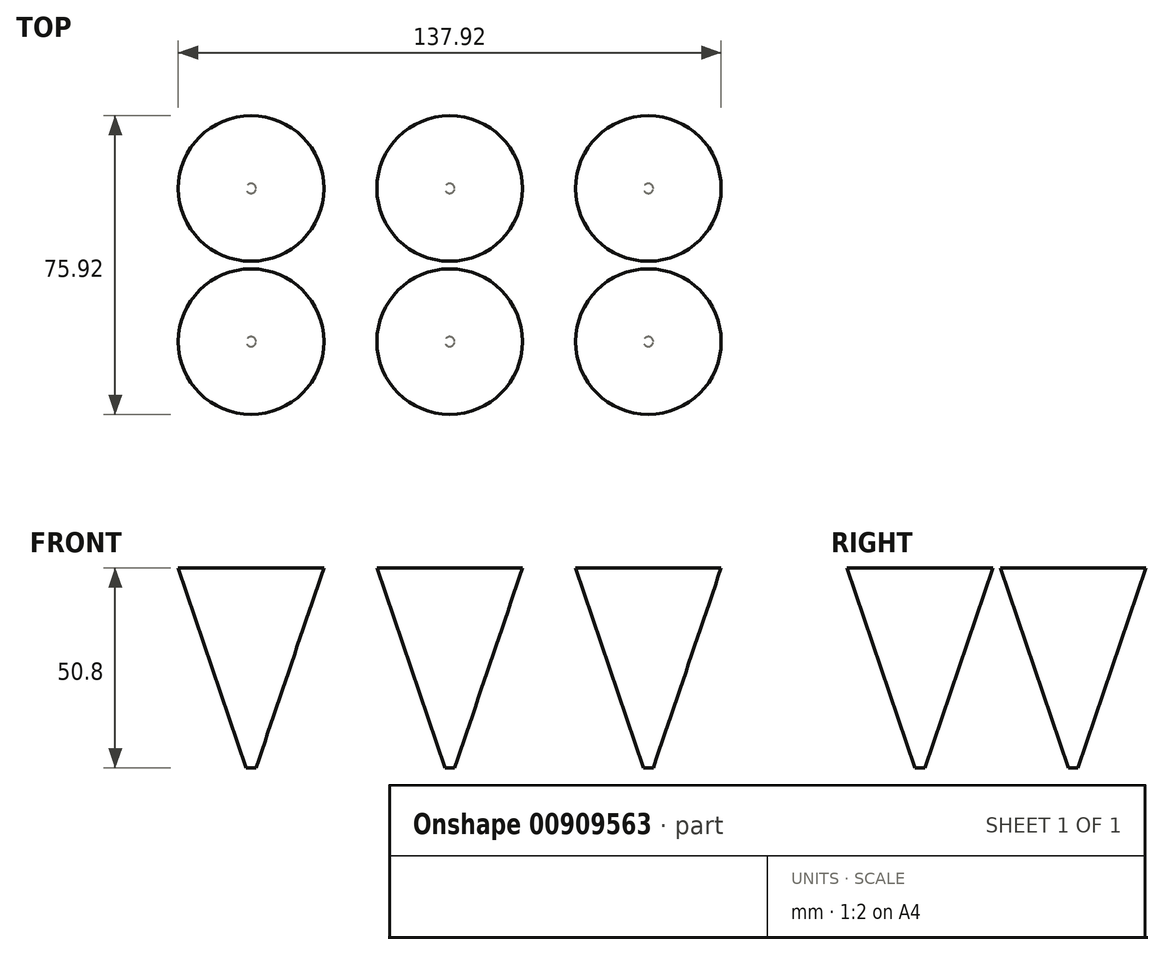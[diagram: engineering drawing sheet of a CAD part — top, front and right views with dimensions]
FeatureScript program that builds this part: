
annotation { "Feature Type Name" : "Feature", "Feature Type Description" : "" }
export const myFeature = defineFeature(function(context is Context, id is Id, definition is map)
    precondition{}
    {
        {
            assignVariable(context, id + "F0", {"name" : "cone_height", "anyValue" : 50.8 * mm});
        }
        {
            var Q0;
            Q0=qCreatedBy(makeId("Top.planeOp"),FACE);
            var sketch = newSketch(context, id + "F1", { "sketchPlane" : qUnion([Q0])});
            skLineSegment(sketch, "E0.bottom", {"start": v(-70.5, 39.5) * mm, "end": v(70.5, 39.5) * mm});
            skLineSegment(sketch, "E0.top", {"start": v(-70.5, -39.5) * mm, "end": v(70.5, -39.5) * mm});
            skLineSegment(sketch, "E0.left", {"start": v(-70.5, 39.5) * mm, "end": v(-70.5, -39.5) * mm});
            skLineSegment(sketch, "E0.right", {"start": v(70.5, 39.5) * mm, "end": v(70.5, -39.5) * mm});
            skPoint(sketch, "E0.middle", {"position": v(0, 0) * mm});
            skSolve(sketch);
        }
        {
            var Q0;
            Q0=qCreatedBy(makeId("Top.planeOp"),FACE);
            var sketch = newSketch(context, id + "F2", { "sketchPlane" : qUnion([Q0])});
            skPoint(sketch, "E1", {"position": v(50.46, 19.46) * mm});
            skPoint(sketch, "E2", {"position": v(0, 19.46) * mm});
            skPoint(sketch, "E3", {"position": v(-50.46, 19.46) * mm});
            skPoint(sketch, "E4", {"position": v(50.46, -19.46) * mm});
            skPoint(sketch, "E5", {"position": v(0, -19.46) * mm});
            skPoint(sketch, "E6", {"position": v(-50.46, -19.46) * mm});
            skCircle(sketch, "E7", {"center": v(50.46, 19.46) * mm, "radius": 18.5 * mm});
            skCircle(sketch, "E8", {"center": v(0, 19.46) * mm, "radius": 18.5 * mm});
            skCircle(sketch, "E9", {"center": v(-50.46, 19.46) * mm, "radius": 18.5 * mm});
            skCircle(sketch, "E10", {"center": v(-50.46, -19.46) * mm, "radius": 18.5 * mm});
            skCircle(sketch, "E11", {"center": v(0, -19.46) * mm, "radius": 18.5 * mm});
            skCircle(sketch, "E12", {"center": v(50.46, -19.46) * mm, "radius": 18.5 * mm});
            skLineSegment(sketch, "E13", {"start": v(-50.46, -19.46) * mm, "end": v(0, -19.46) * mm, "construction": true});
            skLineSegment(sketch, "E14", {"start": v(0, -19.46) * mm, "end": v(50.46, -19.46) * mm, "construction": true});
            skLineSegment(sketch, "E15", {"start": v(50.46, -19.46) * mm, "end": v(50.46, 19.46) * mm, "construction": true});
            skLineSegment(sketch, "E16", {"start": v(50.46, 19.46) * mm, "end": v(0, 19.46) * mm, "construction": true});
            skLineSegment(sketch, "E17", {"start": v(0, 19.46) * mm, "end": v(-50.46, 19.46) * mm, "construction": true});
            skLineSegment(sketch, "E18", {"start": v(-50.46, 19.46) * mm, "end": v(-50.46, -19.46) * mm, "construction": true});
            skLineSegment(sketch, "E19", {"start": v(0, -19.46) * mm, "end": v(0, 19.46) * mm, "construction": true});
            skLineSegment(sketch, "E20.0", {"start": v(-70.5, 39.5) * mm, "end": v(-70.5, -39.5) * mm, "construction": true});
            skLineSegment(sketch, "E20.1", {"start": v(-70.5, -39.5) * mm, "end": v(70.5, -39.5) * mm, "construction": true});
            skLineSegment(sketch, "E20.2", {"start": v(-70.5, 39.5) * mm, "end": v(70.5, 39.5) * mm, "construction": true});
            skLineSegment(sketch, "E20.3", {"start": v(70.5, 39.5) * mm, "end": v(70.5, -39.5) * mm, "construction": true});
            skLineSegment(sketch, "E21", {"start": v(-50.46, -39.5) * mm, "end": v(-50.46, -37.96) * mm, "construction": true});
            skLineSegment(sketch, "E22", {"start": v(-68.96, -19.46) * mm, "end": v(-70.5, -19.46) * mm, "construction": true});
            skSolve(sketch);
        }
        {
            var Q0;
            Q0=qCreatedBy(makeId("Top.planeOp"),FACE);
            cPlane(context, id + "F3", {"entities" : qUnion([Q0]), "cplaneType" : CPlaneType.OFFSET, "offset" : getVariable(context, 'cone_height'), "oppositeDirection" : true, "width" : 150 * mm, "height" : 150 * mm});
        }
        {
            var Q0;
            Q0=qCreatedBy(id+"F3.planeOp",FACE);
            var sketch = newSketch(context, id + "F4", { "sketchPlane" : qUnion([Q0])});
            skPoint(sketch, "E23.0", {"position": v(-50.46, 19.46) * mm});
            skPoint(sketch, "E23.1", {"position": v(-50.46, -19.46) * mm});
            skPoint(sketch, "E23.2", {"position": v(0, -19.46) * mm});
            skPoint(sketch, "E23.3", {"position": v(0, 19.46) * mm});
            skPoint(sketch, "E23.4", {"position": v(50.46, 19.46) * mm});
            skPoint(sketch, "E23.5", {"position": v(50.46, -19.46) * mm});
            skCircle(sketch, "E24", {"center": v(-50.46, -19.46) * mm, "radius": 1.25 * mm});
            skCircle(sketch, "E25", {"center": v(0, -19.46) * mm, "radius": 1.25 * mm});
            skCircle(sketch, "E26", {"center": v(50.46, -19.46) * mm, "radius": 1.25 * mm});
            skCircle(sketch, "E27", {"center": v(50.46, 19.46) * mm, "radius": 1.25 * mm});
            skCircle(sketch, "E28", {"center": v(0, 19.46) * mm, "radius": 1.25 * mm});
            skCircle(sketch, "E29", {"center": v(-50.46, 19.46) * mm, "radius": 1.25 * mm});
            skSolve(sketch);
        }
        {
            var Q0;
            Q0=makeQuery(id+"F4.imprint","IMPRINT",FACE,{"disambiguationData":[TD([[makeQuery(id+"F4.imprint","IMPRINT",EDGE,{"derivedFrom":sQuery(id+"F4.wireOp",EDGE,"E29")}),1.0]])]});
            var Q1;
            Q1=makeQuery(id+"F2.imprint","IMPRINT",FACE,{"disambiguationData":[TD([[makeQuery(id+"F2.imprint","IMPRINT",EDGE,{"derivedFrom":sQuery(id+"F2.wireOp",EDGE,"E9")}),1.0]])]});
            loft(context, id + "F5", {"sheetProfilesArray" : [{ "sheetProfileEntities" : qUnion([Q0]) }, { "sheetProfileEntities" : qUnion([Q1]) }]});
        }
        {
            var Q0;
            Q0=makeQuery(id+"F2.imprint","IMPRINT",FACE,{"disambiguationData":[TD([[makeQuery(id+"F2.imprint","IMPRINT",EDGE,{"derivedFrom":sQuery(id+"F2.wireOp",EDGE,"E8")}),1.0]])]});
            var Q1;
            Q1=makeQuery(id+"F4.imprint","IMPRINT",FACE,{"disambiguationData":[TD([[makeQuery(id+"F4.imprint","IMPRINT",EDGE,{"derivedFrom":sQuery(id+"F4.wireOp",EDGE,"E28")}),1.0]])]});
            loft(context, id + "F6", {"sheetProfilesArray" : [{ "sheetProfileEntities" : qUnion([Q0]) }, { "sheetProfileEntities" : qUnion([Q1]) }]});
        }
        {
            var Q0;
            Q0=makeQuery(id+"F2.imprint","IMPRINT",FACE,{"disambiguationData":[TD([[makeQuery(id+"F2.imprint","IMPRINT",EDGE,{"derivedFrom":sQuery(id+"F2.wireOp",EDGE,"E7")}),1.0]])]});
            var Q1;
            Q1=makeQuery(id+"F4.imprint","IMPRINT",FACE,{"disambiguationData":[TD([[makeQuery(id+"F4.imprint","IMPRINT",EDGE,{"derivedFrom":sQuery(id+"F4.wireOp",EDGE,"E27")}),1.0]])]});
            loft(context, id + "F7", {"sheetProfilesArray" : [{ "sheetProfileEntities" : qUnion([Q0]) }, { "sheetProfileEntities" : qUnion([Q1]) }]});
        }
        {
            var Q0;
            Q0=makeQuery(id+"F4.imprint","IMPRINT",FACE,{"disambiguationData":[TD([[makeQuery(id+"F4.imprint","IMPRINT",EDGE,{"derivedFrom":sQuery(id+"F4.wireOp",EDGE,"E26")}),1.0]])]});
            var Q1;
            Q1=makeQuery(id+"F2.imprint","IMPRINT",FACE,{"disambiguationData":[TD([[makeQuery(id+"F2.imprint","IMPRINT",EDGE,{"derivedFrom":sQuery(id+"F2.wireOp",EDGE,"E12")}),1.0]])]});
            loft(context, id + "F8", {"sheetProfilesArray" : [{ "sheetProfileEntities" : qUnion([Q0]) }, { "sheetProfileEntities" : qUnion([Q1]) }]});
        }
        {
            var Q0;
            Q0=makeQuery(id+"F4.imprint","IMPRINT",FACE,{"disambiguationData":[TD([[makeQuery(id+"F4.imprint","IMPRINT",EDGE,{"derivedFrom":sQuery(id+"F4.wireOp",EDGE,"E25")}),1.0]])]});
            var Q1;
            Q1=makeQuery(id+"F2.imprint","IMPRINT",FACE,{"disambiguationData":[TD([[makeQuery(id+"F2.imprint","IMPRINT",EDGE,{"derivedFrom":sQuery(id+"F2.wireOp",EDGE,"E11")}),1.0]])]});
            loft(context, id + "F9", {"sheetProfilesArray" : [{ "sheetProfileEntities" : qUnion([Q0]) }, { "sheetProfileEntities" : qUnion([Q1]) }]});
        }
        {
            var Q0;
            Q0=makeQuery(id+"F4.imprint","IMPRINT",FACE,{"disambiguationData":[TD([[makeQuery(id+"F4.imprint","IMPRINT",EDGE,{"derivedFrom":sQuery(id+"F4.wireOp",EDGE,"E24")}),1.0]])]});
            var Q1;
            Q1=makeQuery(id+"F2.imprint","IMPRINT",FACE,{"disambiguationData":[TD([[makeQuery(id+"F2.imprint","IMPRINT",EDGE,{"derivedFrom":sQuery(id+"F2.wireOp",EDGE,"E10")}),1.0]])]});
            loft(context, id + "F10", {"sheetProfilesArray" : [{ "sheetProfileEntities" : qUnion([Q0]) }, { "sheetProfileEntities" : qUnion([Q1]) }]});
        }
    });
